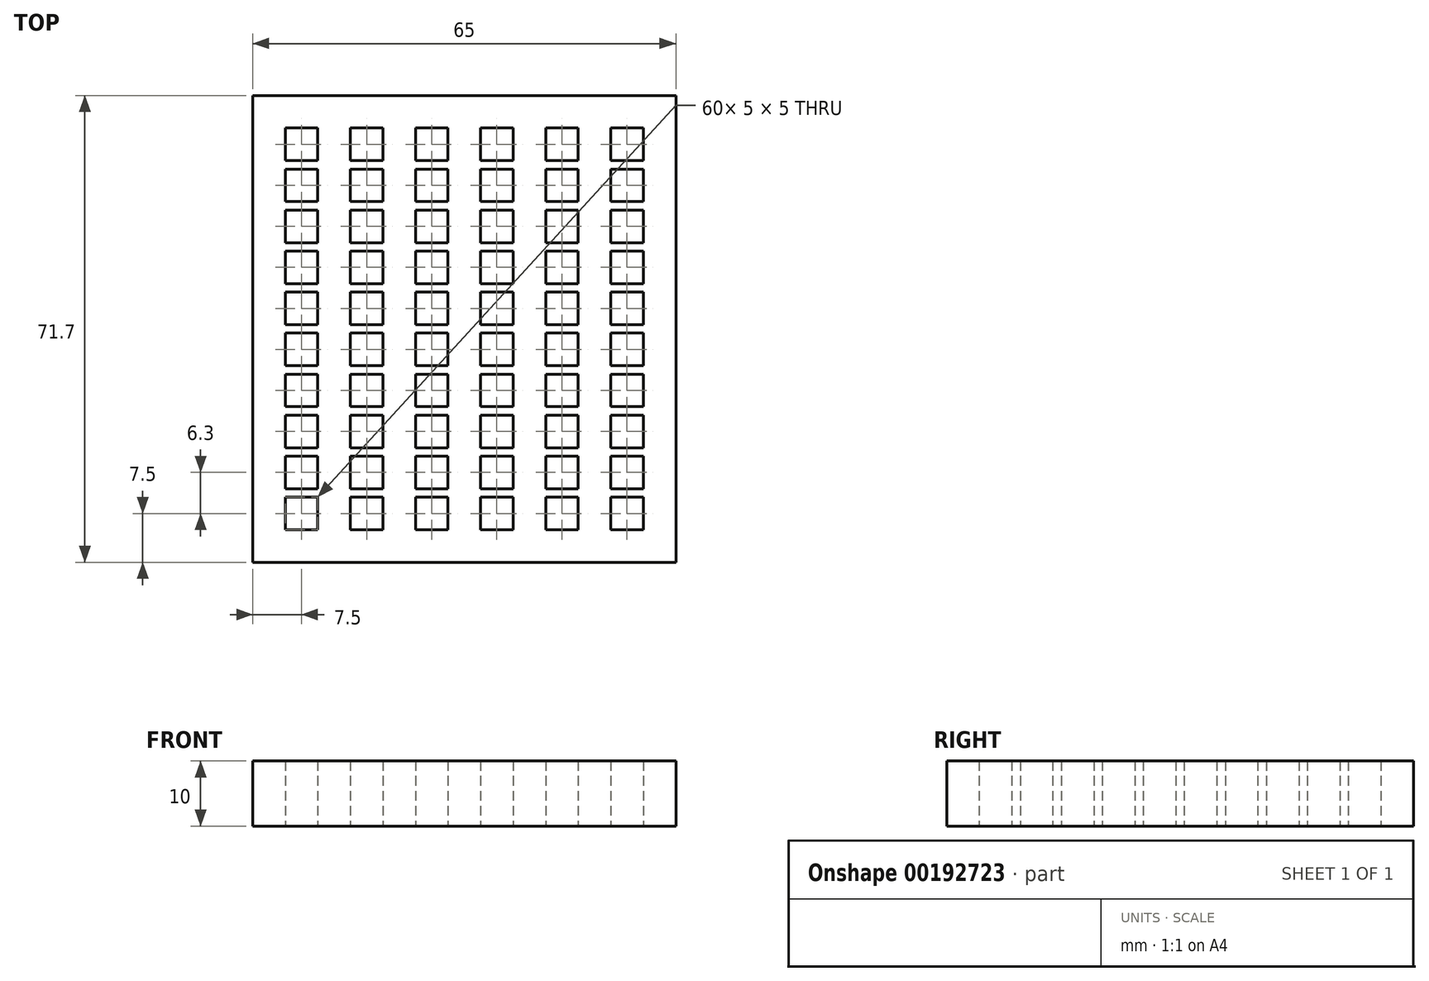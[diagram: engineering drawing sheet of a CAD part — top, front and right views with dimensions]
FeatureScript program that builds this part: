
annotation { "Feature Type Name" : "Feature", "Feature Type Description" : "" }
export const myFeature = defineFeature(function(context is Context, id is Id, definition is map)
    precondition{}
    {
        {
            var Q0;
            Q0=qCreatedBy(makeId("Top.planeOp"),FACE);
            var sketch = newSketch(context, id + "F0", { "sketchPlane" : qUnion([Q0])});
            skLineSegment(sketch, "E0.bottom", {"start": v(0, 0) * mm, "end": v(5, 0) * mm});
            skLineSegment(sketch, "E0.top", {"start": v(0, 5) * mm, "end": v(5, 5) * mm});
            skLineSegment(sketch, "E0.left", {"start": v(0, 0) * mm, "end": v(0, 5) * mm});
            skLineSegment(sketch, "E0.right", {"start": v(5, 0) * mm, "end": v(5, 5) * mm});
            skLineSegment(sketch, "E1.0.1.0", {"start": v(0, 11.3) * mm, "end": v(5, 11.3) * mm});
            skLineSegment(sketch, "E1.0.1.1", {"start": v(0, 6.3) * mm, "end": v(0, 11.3) * mm});
            skLineSegment(sketch, "E1.0.1.2", {"start": v(5, 6.3) * mm, "end": v(5, 11.3) * mm});
            skLineSegment(sketch, "E1.0.1.3", {"start": v(0, 6.3) * mm, "end": v(5, 6.3) * mm});
            skLineSegment(sketch, "E1.1.0.0", {"start": v(10, 5) * mm, "end": v(15, 5) * mm});
            skLineSegment(sketch, "E1.1.0.1", {"start": v(10, 0) * mm, "end": v(10, 5) * mm});
            skLineSegment(sketch, "E1.1.0.2", {"start": v(15, 0) * mm, "end": v(15, 5) * mm});
            skLineSegment(sketch, "E1.1.0.3", {"start": v(10, 0) * mm, "end": v(15, 0) * mm});
            skLineSegment(sketch, "E1.1.1.0", {"start": v(10, 11.3) * mm, "end": v(15, 11.3) * mm});
            skLineSegment(sketch, "E1.1.1.1", {"start": v(10, 6.3) * mm, "end": v(10, 11.3) * mm});
            skLineSegment(sketch, "E1.1.1.2", {"start": v(15, 6.3) * mm, "end": v(15, 11.3) * mm});
            skLineSegment(sketch, "E1.1.1.3", {"start": v(10, 6.3) * mm, "end": v(15, 6.3) * mm});
            skLineSegment(sketch, "E1.2.0.0", {"start": v(20, 5) * mm, "end": v(25, 5) * mm});
            skLineSegment(sketch, "E1.2.0.1", {"start": v(20, 0) * mm, "end": v(20, 5) * mm});
            skLineSegment(sketch, "E1.2.0.2", {"start": v(25, 0) * mm, "end": v(25, 5) * mm});
            skLineSegment(sketch, "E1.2.0.3", {"start": v(20, 0) * mm, "end": v(25, 0) * mm});
            skLineSegment(sketch, "E1.2.1.0", {"start": v(20, 11.3) * mm, "end": v(25, 11.3) * mm});
            skLineSegment(sketch, "E1.2.1.1", {"start": v(20, 6.3) * mm, "end": v(20, 11.3) * mm});
            skLineSegment(sketch, "E1.2.1.2", {"start": v(25, 6.3) * mm, "end": v(25, 11.3) * mm});
            skLineSegment(sketch, "E1.2.1.3", {"start": v(20, 6.3) * mm, "end": v(25, 6.3) * mm});
            skLineSegment(sketch, "E1.direction1", {"start": v(0, 5) * mm, "end": v(10, 5) * mm, "construction": true});
            skLineSegment(sketch, "E1.direction2", {"start": v(0, 5) * mm, "end": v(0, 11.3) * mm, "construction": true});
            skLineSegment(sketch, "E2.0.0.2", {"start": v(0, 17.6) * mm, "end": v(5, 17.6) * mm});
            skLineSegment(sketch, "E2.3.0.2", {"start": v(0, 12.6) * mm, "end": v(0, 17.6) * mm});
            skLineSegment(sketch, "E2.6.0.2", {"start": v(5, 12.6) * mm, "end": v(5, 17.6) * mm});
            skLineSegment(sketch, "E2.9.0.2", {"start": v(0, 12.6) * mm, "end": v(5, 12.6) * mm});
            skLineSegment(sketch, "E2.0.0.3", {"start": v(0, 23.9) * mm, "end": v(5, 23.9) * mm});
            skLineSegment(sketch, "E2.3.0.3", {"start": v(0, 18.9) * mm, "end": v(0, 23.9) * mm});
            skLineSegment(sketch, "E2.6.0.3", {"start": v(5, 18.9) * mm, "end": v(5, 23.9) * mm});
            skLineSegment(sketch, "E2.9.0.3", {"start": v(0, 18.9) * mm, "end": v(5, 18.9) * mm});
            skLineSegment(sketch, "E2.0.0.4", {"start": v(0, 30.2) * mm, "end": v(5, 30.2) * mm});
            skLineSegment(sketch, "E2.3.0.4", {"start": v(0, 25.2) * mm, "end": v(0, 30.2) * mm});
            skLineSegment(sketch, "E2.6.0.4", {"start": v(5, 25.2) * mm, "end": v(5, 30.2) * mm});
            skLineSegment(sketch, "E2.9.0.4", {"start": v(0, 25.2) * mm, "end": v(5, 25.2) * mm});
            skLineSegment(sketch, "E2.0.0.5", {"start": v(0, 36.5) * mm, "end": v(5, 36.5) * mm});
            skLineSegment(sketch, "E2.3.0.5", {"start": v(0, 31.5) * mm, "end": v(0, 36.5) * mm});
            skLineSegment(sketch, "E2.6.0.5", {"start": v(5, 31.5) * mm, "end": v(5, 36.5) * mm});
            skLineSegment(sketch, "E2.9.0.5", {"start": v(0, 31.5) * mm, "end": v(5, 31.5) * mm});
            skLineSegment(sketch, "E2.0.0.6", {"start": v(0, 42.8) * mm, "end": v(5, 42.8) * mm});
            skLineSegment(sketch, "E2.3.0.6", {"start": v(0, 37.8) * mm, "end": v(0, 42.8) * mm});
            skLineSegment(sketch, "E2.6.0.6", {"start": v(5, 37.8) * mm, "end": v(5, 42.8) * mm});
            skLineSegment(sketch, "E2.9.0.6", {"start": v(0, 37.8) * mm, "end": v(5, 37.8) * mm});
            skLineSegment(sketch, "E2.0.0.7", {"start": v(0, 49.1) * mm, "end": v(5, 49.1) * mm});
            skLineSegment(sketch, "E2.3.0.7", {"start": v(0, 44.1) * mm, "end": v(0, 49.1) * mm});
            skLineSegment(sketch, "E2.6.0.7", {"start": v(5, 44.1) * mm, "end": v(5, 49.1) * mm});
            skLineSegment(sketch, "E2.9.0.7", {"start": v(0, 44.1) * mm, "end": v(5, 44.1) * mm});
            skLineSegment(sketch, "E2.0.0.8", {"start": v(0, 55.4) * mm, "end": v(5, 55.4) * mm});
            skLineSegment(sketch, "E2.3.0.8", {"start": v(0, 50.4) * mm, "end": v(0, 55.4) * mm});
            skLineSegment(sketch, "E2.6.0.8", {"start": v(5, 50.4) * mm, "end": v(5, 55.4) * mm});
            skLineSegment(sketch, "E2.9.0.8", {"start": v(0, 50.4) * mm, "end": v(5, 50.4) * mm});
            skLineSegment(sketch, "E2.0.0.9", {"start": v(0, 61.7) * mm, "end": v(5, 61.7) * mm});
            skLineSegment(sketch, "E2.3.0.9", {"start": v(0, 56.7) * mm, "end": v(0, 61.7) * mm});
            skLineSegment(sketch, "E2.6.0.9", {"start": v(5, 56.7) * mm, "end": v(5, 61.7) * mm});
            skLineSegment(sketch, "E2.9.0.9", {"start": v(0, 56.7) * mm, "end": v(5, 56.7) * mm});
            skLineSegment(sketch, "E2.0.1.2", {"start": v(10, 17.6) * mm, "end": v(15, 17.6) * mm});
            skLineSegment(sketch, "E2.3.1.2", {"start": v(10, 12.6) * mm, "end": v(10, 17.6) * mm});
            skLineSegment(sketch, "E2.6.1.2", {"start": v(15, 12.6) * mm, "end": v(15, 17.6) * mm});
            skLineSegment(sketch, "E2.9.1.2", {"start": v(10, 12.6) * mm, "end": v(15, 12.6) * mm});
            skLineSegment(sketch, "E2.0.1.3", {"start": v(10, 23.9) * mm, "end": v(15, 23.9) * mm});
            skLineSegment(sketch, "E2.3.1.3", {"start": v(10, 18.9) * mm, "end": v(10, 23.9) * mm});
            skLineSegment(sketch, "E2.6.1.3", {"start": v(15, 18.9) * mm, "end": v(15, 23.9) * mm});
            skLineSegment(sketch, "E2.9.1.3", {"start": v(10, 18.9) * mm, "end": v(15, 18.9) * mm});
            skLineSegment(sketch, "E2.0.1.4", {"start": v(10, 30.2) * mm, "end": v(15, 30.2) * mm});
            skLineSegment(sketch, "E2.3.1.4", {"start": v(10, 25.2) * mm, "end": v(10, 30.2) * mm});
            skLineSegment(sketch, "E2.6.1.4", {"start": v(15, 25.2) * mm, "end": v(15, 30.2) * mm});
            skLineSegment(sketch, "E2.9.1.4", {"start": v(10, 25.2) * mm, "end": v(15, 25.2) * mm});
            skLineSegment(sketch, "E2.0.1.5", {"start": v(10, 36.5) * mm, "end": v(15, 36.5) * mm});
            skLineSegment(sketch, "E2.3.1.5", {"start": v(10, 31.5) * mm, "end": v(10, 36.5) * mm});
            skLineSegment(sketch, "E2.6.1.5", {"start": v(15, 31.5) * mm, "end": v(15, 36.5) * mm});
            skLineSegment(sketch, "E2.9.1.5", {"start": v(10, 31.5) * mm, "end": v(15, 31.5) * mm});
            skLineSegment(sketch, "E2.0.1.6", {"start": v(10, 42.8) * mm, "end": v(15, 42.8) * mm});
            skLineSegment(sketch, "E2.3.1.6", {"start": v(10, 37.8) * mm, "end": v(10, 42.8) * mm});
            skLineSegment(sketch, "E2.6.1.6", {"start": v(15, 37.8) * mm, "end": v(15, 42.8) * mm});
            skLineSegment(sketch, "E2.9.1.6", {"start": v(10, 37.8) * mm, "end": v(15, 37.8) * mm});
            skLineSegment(sketch, "E2.0.1.7", {"start": v(10, 49.1) * mm, "end": v(15, 49.1) * mm});
            skLineSegment(sketch, "E2.3.1.7", {"start": v(10, 44.1) * mm, "end": v(10, 49.1) * mm});
            skLineSegment(sketch, "E2.6.1.7", {"start": v(15, 44.1) * mm, "end": v(15, 49.1) * mm});
            skLineSegment(sketch, "E2.9.1.7", {"start": v(10, 44.1) * mm, "end": v(15, 44.1) * mm});
            skLineSegment(sketch, "E2.0.1.8", {"start": v(10, 55.4) * mm, "end": v(15, 55.4) * mm});
            skLineSegment(sketch, "E2.3.1.8", {"start": v(10, 50.4) * mm, "end": v(10, 55.4) * mm});
            skLineSegment(sketch, "E2.6.1.8", {"start": v(15, 50.4) * mm, "end": v(15, 55.4) * mm});
            skLineSegment(sketch, "E2.9.1.8", {"start": v(10, 50.4) * mm, "end": v(15, 50.4) * mm});
            skLineSegment(sketch, "E2.0.1.9", {"start": v(10, 61.7) * mm, "end": v(15, 61.7) * mm});
            skLineSegment(sketch, "E2.3.1.9", {"start": v(10, 56.7) * mm, "end": v(10, 61.7) * mm});
            skLineSegment(sketch, "E2.6.1.9", {"start": v(15, 56.7) * mm, "end": v(15, 61.7) * mm});
            skLineSegment(sketch, "E2.9.1.9", {"start": v(10, 56.7) * mm, "end": v(15, 56.7) * mm});
            skLineSegment(sketch, "E2.0.2.2", {"start": v(20, 17.6) * mm, "end": v(25, 17.6) * mm});
            skLineSegment(sketch, "E2.3.2.2", {"start": v(20, 12.6) * mm, "end": v(20, 17.6) * mm});
            skLineSegment(sketch, "E2.6.2.2", {"start": v(25, 12.6) * mm, "end": v(25, 17.6) * mm});
            skLineSegment(sketch, "E2.9.2.2", {"start": v(20, 12.6) * mm, "end": v(25, 12.6) * mm});
            skLineSegment(sketch, "E2.0.2.3", {"start": v(20, 23.9) * mm, "end": v(25, 23.9) * mm});
            skLineSegment(sketch, "E2.3.2.3", {"start": v(20, 18.9) * mm, "end": v(20, 23.9) * mm});
            skLineSegment(sketch, "E2.6.2.3", {"start": v(25, 18.9) * mm, "end": v(25, 23.9) * mm});
            skLineSegment(sketch, "E2.9.2.3", {"start": v(20, 18.9) * mm, "end": v(25, 18.9) * mm});
            skLineSegment(sketch, "E2.0.2.4", {"start": v(20, 30.2) * mm, "end": v(25, 30.2) * mm});
            skLineSegment(sketch, "E2.3.2.4", {"start": v(20, 25.2) * mm, "end": v(20, 30.2) * mm});
            skLineSegment(sketch, "E2.6.2.4", {"start": v(25, 25.2) * mm, "end": v(25, 30.2) * mm});
            skLineSegment(sketch, "E2.9.2.4", {"start": v(20, 25.2) * mm, "end": v(25, 25.2) * mm});
            skLineSegment(sketch, "E2.0.2.5", {"start": v(20, 36.5) * mm, "end": v(25, 36.5) * mm});
            skLineSegment(sketch, "E2.3.2.5", {"start": v(20, 31.5) * mm, "end": v(20, 36.5) * mm});
            skLineSegment(sketch, "E2.6.2.5", {"start": v(25, 31.5) * mm, "end": v(25, 36.5) * mm});
            skLineSegment(sketch, "E2.9.2.5", {"start": v(20, 31.5) * mm, "end": v(25, 31.5) * mm});
            skLineSegment(sketch, "E2.0.2.6", {"start": v(20, 42.8) * mm, "end": v(25, 42.8) * mm});
            skLineSegment(sketch, "E2.3.2.6", {"start": v(20, 37.8) * mm, "end": v(20, 42.8) * mm});
            skLineSegment(sketch, "E2.6.2.6", {"start": v(25, 37.8) * mm, "end": v(25, 42.8) * mm});
            skLineSegment(sketch, "E2.9.2.6", {"start": v(20, 37.8) * mm, "end": v(25, 37.8) * mm});
            skLineSegment(sketch, "E2.0.2.7", {"start": v(20, 49.1) * mm, "end": v(25, 49.1) * mm});
            skLineSegment(sketch, "E2.3.2.7", {"start": v(20, 44.1) * mm, "end": v(20, 49.1) * mm});
            skLineSegment(sketch, "E2.6.2.7", {"start": v(25, 44.1) * mm, "end": v(25, 49.1) * mm});
            skLineSegment(sketch, "E2.9.2.7", {"start": v(20, 44.1) * mm, "end": v(25, 44.1) * mm});
            skLineSegment(sketch, "E2.0.2.8", {"start": v(20, 55.4) * mm, "end": v(25, 55.4) * mm});
            skLineSegment(sketch, "E2.3.2.8", {"start": v(20, 50.4) * mm, "end": v(20, 55.4) * mm});
            skLineSegment(sketch, "E2.6.2.8", {"start": v(25, 50.4) * mm, "end": v(25, 55.4) * mm});
            skLineSegment(sketch, "E2.9.2.8", {"start": v(20, 50.4) * mm, "end": v(25, 50.4) * mm});
            skLineSegment(sketch, "E2.0.2.9", {"start": v(20, 61.7) * mm, "end": v(25, 61.7) * mm});
            skLineSegment(sketch, "E2.3.2.9", {"start": v(20, 56.7) * mm, "end": v(20, 61.7) * mm});
            skLineSegment(sketch, "E2.6.2.9", {"start": v(25, 56.7) * mm, "end": v(25, 61.7) * mm});
            skLineSegment(sketch, "E2.9.2.9", {"start": v(20, 56.7) * mm, "end": v(25, 56.7) * mm});
            skLineSegment(sketch, "E3.0.3.0", {"start": v(30, 5) * mm, "end": v(35, 5) * mm});
            skLineSegment(sketch, "E3.3.3.0", {"start": v(30, 0) * mm, "end": v(30, 5) * mm});
            skLineSegment(sketch, "E3.6.3.0", {"start": v(35, 0) * mm, "end": v(35, 5) * mm});
            skLineSegment(sketch, "E3.9.3.0", {"start": v(30, 0) * mm, "end": v(35, 0) * mm});
            skLineSegment(sketch, "E3.0.3.1", {"start": v(30, 11.3) * mm, "end": v(35, 11.3) * mm});
            skLineSegment(sketch, "E3.3.3.1", {"start": v(30, 6.3) * mm, "end": v(30, 11.3) * mm});
            skLineSegment(sketch, "E3.6.3.1", {"start": v(35, 6.3) * mm, "end": v(35, 11.3) * mm});
            skLineSegment(sketch, "E3.9.3.1", {"start": v(30, 6.3) * mm, "end": v(35, 6.3) * mm});
            skLineSegment(sketch, "E3.0.3.2", {"start": v(30, 17.6) * mm, "end": v(35, 17.6) * mm});
            skLineSegment(sketch, "E3.3.3.2", {"start": v(30, 12.6) * mm, "end": v(30, 17.6) * mm});
            skLineSegment(sketch, "E3.6.3.2", {"start": v(35, 12.6) * mm, "end": v(35, 17.6) * mm});
            skLineSegment(sketch, "E3.9.3.2", {"start": v(30, 12.6) * mm, "end": v(35, 12.6) * mm});
            skLineSegment(sketch, "E3.0.3.3", {"start": v(30, 23.9) * mm, "end": v(35, 23.9) * mm});
            skLineSegment(sketch, "E3.3.3.3", {"start": v(30, 18.9) * mm, "end": v(30, 23.9) * mm});
            skLineSegment(sketch, "E3.6.3.3", {"start": v(35, 18.9) * mm, "end": v(35, 23.9) * mm});
            skLineSegment(sketch, "E3.9.3.3", {"start": v(30, 18.9) * mm, "end": v(35, 18.9) * mm});
            skLineSegment(sketch, "E3.0.3.4", {"start": v(30, 30.2) * mm, "end": v(35, 30.2) * mm});
            skLineSegment(sketch, "E3.3.3.4", {"start": v(30, 25.2) * mm, "end": v(30, 30.2) * mm});
            skLineSegment(sketch, "E3.6.3.4", {"start": v(35, 25.2) * mm, "end": v(35, 30.2) * mm});
            skLineSegment(sketch, "E3.9.3.4", {"start": v(30, 25.2) * mm, "end": v(35, 25.2) * mm});
            skLineSegment(sketch, "E3.0.3.5", {"start": v(30, 36.5) * mm, "end": v(35, 36.5) * mm});
            skLineSegment(sketch, "E3.3.3.5", {"start": v(30, 31.5) * mm, "end": v(30, 36.5) * mm});
            skLineSegment(sketch, "E3.6.3.5", {"start": v(35, 31.5) * mm, "end": v(35, 36.5) * mm});
            skLineSegment(sketch, "E3.9.3.5", {"start": v(30, 31.5) * mm, "end": v(35, 31.5) * mm});
            skLineSegment(sketch, "E3.0.3.6", {"start": v(30, 42.8) * mm, "end": v(35, 42.8) * mm});
            skLineSegment(sketch, "E3.3.3.6", {"start": v(30, 37.8) * mm, "end": v(30, 42.8) * mm});
            skLineSegment(sketch, "E3.6.3.6", {"start": v(35, 37.8) * mm, "end": v(35, 42.8) * mm});
            skLineSegment(sketch, "E3.9.3.6", {"start": v(30, 37.8) * mm, "end": v(35, 37.8) * mm});
            skLineSegment(sketch, "E3.0.3.7", {"start": v(30, 49.1) * mm, "end": v(35, 49.1) * mm});
            skLineSegment(sketch, "E3.3.3.7", {"start": v(30, 44.1) * mm, "end": v(30, 49.1) * mm});
            skLineSegment(sketch, "E3.6.3.7", {"start": v(35, 44.1) * mm, "end": v(35, 49.1) * mm});
            skLineSegment(sketch, "E3.9.3.7", {"start": v(30, 44.1) * mm, "end": v(35, 44.1) * mm});
            skLineSegment(sketch, "E3.0.3.8", {"start": v(30, 55.4) * mm, "end": v(35, 55.4) * mm});
            skLineSegment(sketch, "E3.3.3.8", {"start": v(30, 50.4) * mm, "end": v(30, 55.4) * mm});
            skLineSegment(sketch, "E3.6.3.8", {"start": v(35, 50.4) * mm, "end": v(35, 55.4) * mm});
            skLineSegment(sketch, "E3.9.3.8", {"start": v(30, 50.4) * mm, "end": v(35, 50.4) * mm});
            skLineSegment(sketch, "E3.0.3.9", {"start": v(30, 61.7) * mm, "end": v(35, 61.7) * mm});
            skLineSegment(sketch, "E3.3.3.9", {"start": v(30, 56.7) * mm, "end": v(30, 61.7) * mm});
            skLineSegment(sketch, "E3.6.3.9", {"start": v(35, 56.7) * mm, "end": v(35, 61.7) * mm});
            skLineSegment(sketch, "E3.9.3.9", {"start": v(30, 56.7) * mm, "end": v(35, 56.7) * mm});
            skLineSegment(sketch, "E3.0.4.0", {"start": v(40, 5) * mm, "end": v(45, 5) * mm});
            skLineSegment(sketch, "E3.3.4.0", {"start": v(40, 0) * mm, "end": v(40, 5) * mm});
            skLineSegment(sketch, "E3.6.4.0", {"start": v(45, 0) * mm, "end": v(45, 5) * mm});
            skLineSegment(sketch, "E3.9.4.0", {"start": v(40, 0) * mm, "end": v(45, 0) * mm});
            skLineSegment(sketch, "E3.0.4.1", {"start": v(40, 11.3) * mm, "end": v(45, 11.3) * mm});
            skLineSegment(sketch, "E3.3.4.1", {"start": v(40, 6.3) * mm, "end": v(40, 11.3) * mm});
            skLineSegment(sketch, "E3.6.4.1", {"start": v(45, 6.3) * mm, "end": v(45, 11.3) * mm});
            skLineSegment(sketch, "E3.9.4.1", {"start": v(40, 6.3) * mm, "end": v(45, 6.3) * mm});
            skLineSegment(sketch, "E3.0.4.2", {"start": v(40, 17.6) * mm, "end": v(45, 17.6) * mm});
            skLineSegment(sketch, "E3.3.4.2", {"start": v(40, 12.6) * mm, "end": v(40, 17.6) * mm});
            skLineSegment(sketch, "E3.6.4.2", {"start": v(45, 12.6) * mm, "end": v(45, 17.6) * mm});
            skLineSegment(sketch, "E3.9.4.2", {"start": v(40, 12.6) * mm, "end": v(45, 12.6) * mm});
            skLineSegment(sketch, "E3.0.4.3", {"start": v(40, 23.9) * mm, "end": v(45, 23.9) * mm});
            skLineSegment(sketch, "E3.3.4.3", {"start": v(40, 18.9) * mm, "end": v(40, 23.9) * mm});
            skLineSegment(sketch, "E3.6.4.3", {"start": v(45, 18.9) * mm, "end": v(45, 23.9) * mm});
            skLineSegment(sketch, "E3.9.4.3", {"start": v(40, 18.9) * mm, "end": v(45, 18.9) * mm});
            skLineSegment(sketch, "E3.0.4.4", {"start": v(40, 30.2) * mm, "end": v(45, 30.2) * mm});
            skLineSegment(sketch, "E3.3.4.4", {"start": v(40, 25.2) * mm, "end": v(40, 30.2) * mm});
            skLineSegment(sketch, "E3.6.4.4", {"start": v(45, 25.2) * mm, "end": v(45, 30.2) * mm});
            skLineSegment(sketch, "E3.9.4.4", {"start": v(40, 25.2) * mm, "end": v(45, 25.2) * mm});
            skLineSegment(sketch, "E3.0.4.5", {"start": v(40, 36.5) * mm, "end": v(45, 36.5) * mm});
            skLineSegment(sketch, "E3.3.4.5", {"start": v(40, 31.5) * mm, "end": v(40, 36.5) * mm});
            skLineSegment(sketch, "E3.6.4.5", {"start": v(45, 31.5) * mm, "end": v(45, 36.5) * mm});
            skLineSegment(sketch, "E3.9.4.5", {"start": v(40, 31.5) * mm, "end": v(45, 31.5) * mm});
            skLineSegment(sketch, "E3.0.4.6", {"start": v(40, 42.8) * mm, "end": v(45, 42.8) * mm});
            skLineSegment(sketch, "E3.3.4.6", {"start": v(40, 37.8) * mm, "end": v(40, 42.8) * mm});
            skLineSegment(sketch, "E3.6.4.6", {"start": v(45, 37.8) * mm, "end": v(45, 42.8) * mm});
            skLineSegment(sketch, "E3.9.4.6", {"start": v(40, 37.8) * mm, "end": v(45, 37.8) * mm});
            skLineSegment(sketch, "E3.0.4.7", {"start": v(40, 49.1) * mm, "end": v(45, 49.1) * mm});
            skLineSegment(sketch, "E3.3.4.7", {"start": v(40, 44.1) * mm, "end": v(40, 49.1) * mm});
            skLineSegment(sketch, "E3.6.4.7", {"start": v(45, 44.1) * mm, "end": v(45, 49.1) * mm});
            skLineSegment(sketch, "E3.9.4.7", {"start": v(40, 44.1) * mm, "end": v(45, 44.1) * mm});
            skLineSegment(sketch, "E3.0.4.8", {"start": v(40, 55.4) * mm, "end": v(45, 55.4) * mm});
            skLineSegment(sketch, "E3.3.4.8", {"start": v(40, 50.4) * mm, "end": v(40, 55.4) * mm});
            skLineSegment(sketch, "E3.6.4.8", {"start": v(45, 50.4) * mm, "end": v(45, 55.4) * mm});
            skLineSegment(sketch, "E3.9.4.8", {"start": v(40, 50.4) * mm, "end": v(45, 50.4) * mm});
            skLineSegment(sketch, "E3.0.4.9", {"start": v(40, 61.7) * mm, "end": v(45, 61.7) * mm});
            skLineSegment(sketch, "E3.3.4.9", {"start": v(40, 56.7) * mm, "end": v(40, 61.7) * mm});
            skLineSegment(sketch, "E3.6.4.9", {"start": v(45, 56.7) * mm, "end": v(45, 61.7) * mm});
            skLineSegment(sketch, "E3.9.4.9", {"start": v(40, 56.7) * mm, "end": v(45, 56.7) * mm});
            skLineSegment(sketch, "E3.0.5.0", {"start": v(50, 5) * mm, "end": v(55, 5) * mm});
            skLineSegment(sketch, "E3.3.5.0", {"start": v(50, 0) * mm, "end": v(50, 5) * mm});
            skLineSegment(sketch, "E3.6.5.0", {"start": v(55, 0) * mm, "end": v(55, 5) * mm});
            skLineSegment(sketch, "E3.9.5.0", {"start": v(50, 0) * mm, "end": v(55, 0) * mm});
            skLineSegment(sketch, "E3.0.5.1", {"start": v(50, 11.3) * mm, "end": v(55, 11.3) * mm});
            skLineSegment(sketch, "E3.3.5.1", {"start": v(50, 6.3) * mm, "end": v(50, 11.3) * mm});
            skLineSegment(sketch, "E3.6.5.1", {"start": v(55, 6.3) * mm, "end": v(55, 11.3) * mm});
            skLineSegment(sketch, "E3.9.5.1", {"start": v(50, 6.3) * mm, "end": v(55, 6.3) * mm});
            skLineSegment(sketch, "E3.0.5.2", {"start": v(50, 17.6) * mm, "end": v(55, 17.6) * mm});
            skLineSegment(sketch, "E3.3.5.2", {"start": v(50, 12.6) * mm, "end": v(50, 17.6) * mm});
            skLineSegment(sketch, "E3.6.5.2", {"start": v(55, 12.6) * mm, "end": v(55, 17.6) * mm});
            skLineSegment(sketch, "E3.9.5.2", {"start": v(50, 12.6) * mm, "end": v(55, 12.6) * mm});
            skLineSegment(sketch, "E3.0.5.3", {"start": v(50, 23.9) * mm, "end": v(55, 23.9) * mm});
            skLineSegment(sketch, "E3.3.5.3", {"start": v(50, 18.9) * mm, "end": v(50, 23.9) * mm});
            skLineSegment(sketch, "E3.6.5.3", {"start": v(55, 18.9) * mm, "end": v(55, 23.9) * mm});
            skLineSegment(sketch, "E3.9.5.3", {"start": v(50, 18.9) * mm, "end": v(55, 18.9) * mm});
            skLineSegment(sketch, "E3.0.5.4", {"start": v(50, 30.2) * mm, "end": v(55, 30.2) * mm});
            skLineSegment(sketch, "E3.3.5.4", {"start": v(50, 25.2) * mm, "end": v(50, 30.2) * mm});
            skLineSegment(sketch, "E3.6.5.4", {"start": v(55, 25.2) * mm, "end": v(55, 30.2) * mm});
            skLineSegment(sketch, "E3.9.5.4", {"start": v(50, 25.2) * mm, "end": v(55, 25.2) * mm});
            skLineSegment(sketch, "E3.0.5.5", {"start": v(50, 36.5) * mm, "end": v(55, 36.5) * mm});
            skLineSegment(sketch, "E3.3.5.5", {"start": v(50, 31.5) * mm, "end": v(50, 36.5) * mm});
            skLineSegment(sketch, "E3.6.5.5", {"start": v(55, 31.5) * mm, "end": v(55, 36.5) * mm});
            skLineSegment(sketch, "E3.9.5.5", {"start": v(50, 31.5) * mm, "end": v(55, 31.5) * mm});
            skLineSegment(sketch, "E3.0.5.6", {"start": v(50, 42.8) * mm, "end": v(55, 42.8) * mm});
            skLineSegment(sketch, "E3.3.5.6", {"start": v(50, 37.8) * mm, "end": v(50, 42.8) * mm});
            skLineSegment(sketch, "E3.6.5.6", {"start": v(55, 37.8) * mm, "end": v(55, 42.8) * mm});
            skLineSegment(sketch, "E3.9.5.6", {"start": v(50, 37.8) * mm, "end": v(55, 37.8) * mm});
            skLineSegment(sketch, "E3.0.5.7", {"start": v(50, 49.1) * mm, "end": v(55, 49.1) * mm});
            skLineSegment(sketch, "E3.3.5.7", {"start": v(50, 44.1) * mm, "end": v(50, 49.1) * mm});
            skLineSegment(sketch, "E3.6.5.7", {"start": v(55, 44.1) * mm, "end": v(55, 49.1) * mm});
            skLineSegment(sketch, "E3.9.5.7", {"start": v(50, 44.1) * mm, "end": v(55, 44.1) * mm});
            skLineSegment(sketch, "E3.0.5.8", {"start": v(50, 55.4) * mm, "end": v(55, 55.4) * mm});
            skLineSegment(sketch, "E3.3.5.8", {"start": v(50, 50.4) * mm, "end": v(50, 55.4) * mm});
            skLineSegment(sketch, "E3.6.5.8", {"start": v(55, 50.4) * mm, "end": v(55, 55.4) * mm});
            skLineSegment(sketch, "E3.9.5.8", {"start": v(50, 50.4) * mm, "end": v(55, 50.4) * mm});
            skLineSegment(sketch, "E3.0.5.9", {"start": v(50, 61.7) * mm, "end": v(55, 61.7) * mm});
            skLineSegment(sketch, "E3.3.5.9", {"start": v(50, 56.7) * mm, "end": v(50, 61.7) * mm});
            skLineSegment(sketch, "E3.6.5.9", {"start": v(55, 56.7) * mm, "end": v(55, 61.7) * mm});
            skLineSegment(sketch, "E3.9.5.9", {"start": v(50, 56.7) * mm, "end": v(55, 56.7) * mm});
            skLineSegment(sketch, "E4.right", {"start": v(-5, 66.7) * mm, "end": v(-5, -5) * mm});
            skPoint(sketch, "E4.middle", {"position": v(30, 30.85) * mm});
            skLineSegment(sketch, "E5", {"start": v(-5, 66.7) * mm, "end": v(60, 66.7) * mm});
            skLineSegment(sketch, "E6", {"start": v(60, 66.7) * mm, "end": v(60, -5) * mm});
            skLineSegment(sketch, "E7", {"start": v(60, -5) * mm, "end": v(-5, -5) * mm});
            skSolve(sketch);
        }
        {
            var Q0;
            Q0 = qSketchRegion(id + "F0", true);
            extrude(context, id + "F1", {"entities" : qUnion([Q0]), "depth" : 10 * mm});
        }
    });
